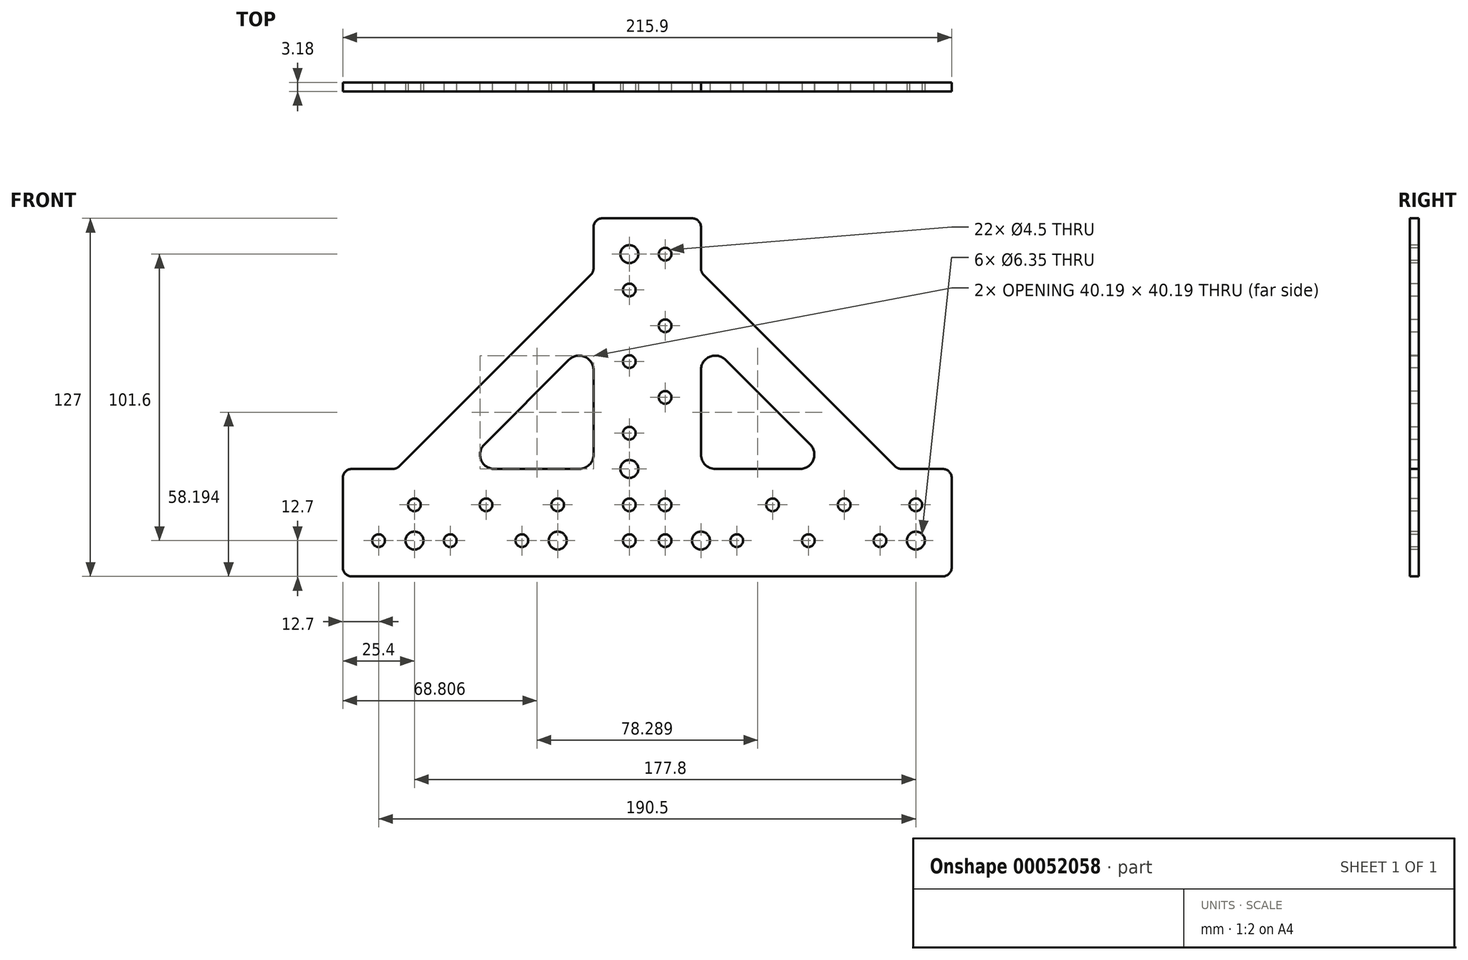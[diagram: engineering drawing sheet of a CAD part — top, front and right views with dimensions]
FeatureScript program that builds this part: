
annotation { "Feature Type Name" : "Feature", "Feature Type Description" : "" }
export const myFeature = defineFeature(function(context is Context, id is Id, definition is map)
    precondition{}
    {
        {
            var Q0;
            Q0=qCreatedBy(makeId("Front.planeOp"),FACE);
            var sketch = newSketch(context, id + "F0", { "sketchPlane" : qUnion([Q0])});
            skLineSegment(sketch, "E0.rect.bottom", {"start": v(-63.5, 63.5) * mm, "end": v(-25.4, 63.5) * mm});
            skLineSegment(sketch, "E0.rect.top", {"start": v(-63.5, -63.5) * mm, "end": v(63.5, -63.5) * mm});
            skLineSegment(sketch, "E0.rect.left", {"start": v(-63.5, 63.5) * mm, "end": v(-63.5, 44.45) * mm});
            skLineSegment(sketch, "E0.rect.right", {"start": v(63.5, -25.4) * mm, "end": v(63.5, -63.5) * mm});
            skPoint(sketch, "E0.rect.middle", {"position": v(0, 0) * mm});
            skLineSegment(sketch, "E1", {"start": v(-25.4, 63.5) * mm, "end": v(-25.4, 44.45) * mm});
            skLineSegment(sketch, "E2", {"start": v(63.5, -25.4) * mm, "end": v(44.45, -25.4) * mm});
            skLineSegment(sketch, "E3", {"start": v(-25.4, 44.45) * mm, "end": v(44.45, -25.4) * mm});
            skLineSegment(sketch, "E4", {"start": v(-25.4, 22) * mm, "end": v(22, -25.4) * mm});
            skPoint(sketch, "E5.orphan", {"position": v(63.5, 63.5) * mm});
            skLineSegment(sketch, "E6.trimOffspring", {"start": v(-25.4, 22) * mm, "end": v(-25.4, -25.4) * mm});
            skLineSegment(sketch, "E7.trimOffspring", {"start": v(22, -25.4) * mm, "end": v(-25.4, -25.4) * mm});
            skLineSegment(sketch, "E8", {"start": v(-63.5, -25.4) * mm, "end": v(-110.9, -25.4) * mm});
            skLineSegment(sketch, "E9", {"start": v(-152.4, -25.4) * mm, "end": v(-152.4, -63.5) * mm});
            skLineSegment(sketch, "E10", {"start": v(-152.4, -63.5) * mm, "end": v(-63.5, -63.5) * mm});
            skLineSegment(sketch, "E11", {"start": v(-63.5, 44.45) * mm, "end": v(-133.35, -25.4) * mm});
            skLineSegment(sketch, "E12", {"start": v(-63.5, 22) * mm, "end": v(-110.9, -25.4) * mm});
            skLineSegment(sketch, "E13.trimOffspring", {"start": v(-63.5, 22) * mm, "end": v(-63.5, -25.4) * mm});
            skLineSegment(sketch, "E14.trimOffspring", {"start": v(-133.35, -25.4) * mm, "end": v(-152.4, -25.4) * mm});
            skSolve(sketch);
        }
        {
            var Q0;
            Q0=makeQuery(id+"F0.imprint","IMPRINT",FACE,{"disambiguationData":[TD([[makeQuery(id+"F0.imprint","IMPRINT",EDGE,{"derivedFrom":sQuery(id+"F0.wireOp",EDGE,"E0.rect.bottom")}),-1.0]])]});
            extrude(context, id + "F1", {"entities" : qUnion([Q0]), "depth" : 3.17 * mm});
        }
        {
            var Q0;
            Q0=makeQuery(id+"F1.opExtrude","SWEPT_EDGE",EDGE,{"disambiguationData":[OSD([sQuery(id+"F0.wireOp",EDGE,"E0.rect.bottom"),sQuery(id+"F0.wireOp",EDGE,"E1")])]});
            var Q1;
            Q1=makeQuery(id+"F1.opExtrude","SWEPT_EDGE",EDGE,{"disambiguationData":[OSD([sQuery(id+"F0.wireOp",EDGE,"E1"),sQuery(id+"F0.wireOp",EDGE,"E3")])]});
            var Q2;
            Q2=makeQuery(id+"F1.opExtrude","SWEPT_EDGE",EDGE,{"disambiguationData":[OSD([sQuery(id+"F0.wireOp",EDGE,"E2"),sQuery(id+"F0.wireOp",EDGE,"E3")])]});
            var Q3;
            Q3=makeQuery(id+"F1.opExtrude","SWEPT_EDGE",EDGE,{"disambiguationData":[OSD([sQuery(id+"F0.wireOp",EDGE,"E0.rect.right"),sQuery(id+"F0.wireOp",EDGE,"E2")])]});
            var Q4;
            Q4=makeQuery(id+"F1.opExtrude","SWEPT_EDGE",EDGE,{"disambiguationData":[OSD([sQuery(id+"F0.wireOp",EDGE,"E0.rect.top"),sQuery(id+"F0.wireOp",EDGE,"E0.rect.right")])]});
            var Q5;
            Q5=makeQuery(id+"F1.opExtrude","SWEPT_EDGE",EDGE,{"disambiguationData":[OSD([sQuery(id+"F0.wireOp",EDGE,"E0.rect.top"),sQuery(id+"F0.wireOp",EDGE,"E0.rect.left")])]});
            var Q6;
            Q6=makeQuery(id+"F1.opExtrude","SWEPT_EDGE",EDGE,{"disambiguationData":[OSD([sQuery(id+"F0.wireOp",EDGE,"E0.rect.bottom"),sQuery(id+"F0.wireOp",EDGE,"E0.rect.left")])]});
            var Q7;
            Q7=makeQuery(id+"F1.opExtrude","SWEPT_EDGE",EDGE,{"disambiguationData":[OSD([sQuery(id+"F0.wireOp",EDGE,"E11"),sQuery(id+"F0.wireOp",EDGE,"E14.trimOffspring")])]});
            var Q8;
            Q8=makeQuery(id+"F1.opExtrude","SWEPT_EDGE",EDGE,{"disambiguationData":[OSD([sQuery(id+"F0.wireOp",EDGE,"E9"),sQuery(id+"F0.wireOp",EDGE,"E14.trimOffspring")])]});
            var Q9;
            Q9=makeQuery(id+"F1.opExtrude","SWEPT_EDGE",EDGE,{"disambiguationData":[OSD([sQuery(id+"F0.wireOp",EDGE,"E9"),sQuery(id+"F0.wireOp",EDGE,"E10")])]});
            fillet(context, id + "F2", {"entities" : qUnion([Q0, Q1, Q2, Q3, Q4, Q5, Q6, Q7, Q8, Q9]), "radius" : 3.17 * mm, "tangentPropagation" : true, "allowEdgeOverflow" : false});
        }
        {
            var Q0;
            Q0=makeQuery(id+"F1.opExtrude","SWEPT_EDGE",EDGE,{"disambiguationData":[OSD([sQuery(id+"F0.wireOp",EDGE,"E4"),sQuery(id+"F0.wireOp",EDGE,"E7.trimOffspring")])]});
            var Q1;
            Q1=makeQuery(id+"F1.opExtrude","SWEPT_EDGE",EDGE,{"disambiguationData":[OSD([sQuery(id+"F0.wireOp",EDGE,"E6.trimOffspring"),sQuery(id+"F0.wireOp",EDGE,"E7.trimOffspring")])]});
            var Q2;
            Q2=makeQuery(id+"F1.opExtrude","SWEPT_EDGE",EDGE,{"disambiguationData":[OSD([sQuery(id+"F0.wireOp",EDGE,"E4"),sQuery(id+"F0.wireOp",EDGE,"E6.trimOffspring")])]});
            fillet(context, id + "F3", {"entities" : qUnion([Q0, Q1, Q2]), "radius" : 5.08 * mm, "tangentPropagation" : true, "allowEdgeOverflow" : false});
        }
        {
            var Q0;
            Q0=makeQuery(id+"F1.opExtrude","CAP_FACE",FACE,{"disambiguationData":[OSD([sQuery(id+"F0.wireOp",EDGE,"E0.rect.bottom"),sQuery(id+"F0.wireOp",EDGE,"E0.rect.top"),sQuery(id+"F0.wireOp",EDGE,"E0.rect.left"),sQuery(id+"F0.wireOp",EDGE,"E0.rect.right"),sQuery(id+"F0.wireOp",EDGE,"E1"),sQuery(id+"F0.wireOp",EDGE,"E2"),sQuery(id+"F0.wireOp",EDGE,"E3"),sQuery(id+"F0.wireOp",EDGE,"E4"),sQuery(id+"F0.wireOp",EDGE,"E6.trimOffspring"),sQuery(id+"F0.wireOp",EDGE,"E7.trimOffspring")])],"isStart":false});
            var sketch = newSketch(context, id + "F4", { "sketchPlane" : qUnion([Q0])});
            skLineSegment(sketch, "E15", {"start": v(-50.8, 66.32) * mm, "end": v(-50.8, -65.15) * mm, "construction": true});
            skLineSegment(sketch, "E16", {"start": v(65.1, -50.8) * mm, "end": v(-158.46, -50.8) * mm, "construction": true});
            skLineSegment(sketch, "E17", {"start": v(-38.1, 66.32) * mm, "end": v(-38.1, -66.32) * mm, "construction": true});
            skLineSegment(sketch, "E18", {"start": v(73.12, -38.1) * mm, "end": v(-159.28, -38.1) * mm, "construction": true});
            skPoint(sketch, "E19", {"position": v(-50.8, -50.8) * mm});
            skPoint(sketch, "E20", {"position": v(-50.8, -38.1) * mm});
            skPoint(sketch, "E21", {"position": v(-38.1, -38.1) * mm});
            skPoint(sketch, "E22", {"position": v(-38.1, -50.8) * mm});
            skPoint(sketch, "E23", {"position": v(-50.8, 50.8) * mm});
            skPoint(sketch, "E24", {"position": v(-38.1, 50.8) * mm});
            skPoint(sketch, "E25", {"position": v(-50.8, 38.1) * mm});
            skPoint(sketch, "E26", {"position": v(-38.1, 25.4) * mm});
            skPoint(sketch, "E27", {"position": v(-50.8, 12.7) * mm});
            skPoint(sketch, "E28", {"position": v(-38.1, 0) * mm});
            skPoint(sketch, "E29", {"position": v(-50.8, -12.7) * mm});
            skPoint(sketch, "E30", {"position": v(-50.8, -25.4) * mm});
            skPoint(sketch, "E31", {"position": v(50.8, -50.8) * mm});
            skPoint(sketch, "E32", {"position": v(50.8, -38.1) * mm});
            skPoint(sketch, "E33", {"position": v(38.1, -50.8) * mm});
            skPoint(sketch, "E34", {"position": v(12.7, -50.8) * mm});
            skPoint(sketch, "E35", {"position": v(-12.7, -50.8) * mm});
            skPoint(sketch, "E36", {"position": v(-25.4, -50.8) * mm});
            skPoint(sketch, "E37", {"position": v(25.4, -38.1) * mm});
            skPoint(sketch, "E38", {"position": v(0, -38.1) * mm});
            skPoint(sketch, "E39", {"position": v(-127, -38.1) * mm});
            skPoint(sketch, "E40", {"position": v(-139.7, -50.8) * mm});
            skPoint(sketch, "E41", {"position": v(-101.6, -38.1) * mm});
            skPoint(sketch, "E42", {"position": v(-76.2, -38.1) * mm});
            skPoint(sketch, "E43", {"position": v(-127, -50.8) * mm});
            skPoint(sketch, "E44", {"position": v(-88.9, -50.8) * mm});
            skPoint(sketch, "E45", {"position": v(-76.2, -50.8) * mm});
            skPoint(sketch, "E46", {"position": v(-114.3, -50.8) * mm});
            skSolve(sketch);
        }
        {
            var Q0;
            Q0=sQuery(id+"F4.wireOp",VERTEX,"E23");
            var Q1;
            Q1=sQuery(id+"F4.wireOp",VERTEX,"E30");
            var Q2;
            Q2=sQuery(id+"F4.wireOp",VERTEX,"E31");
            var Q3;
            Q3=sQuery(id+"F4.wireOp",VERTEX,"E36");
            var Q4;
            Q4=sQuery(id+"F4.wireOp",VERTEX,"E45");
            var Q5;
            Q5=sQuery(id+"F4.wireOp",VERTEX,"E43");
            var Q6;
            Q6=makeQuery(id+"F1.opExtrude","SWEPT_BODY",BODY,{"disambiguationData":[OSD([sQuery(id+"F0.wireOp",EDGE,"E0.rect.bottom"),sQuery(id+"F0.wireOp",EDGE,"E0.rect.top"),sQuery(id+"F0.wireOp",EDGE,"E0.rect.left"),sQuery(id+"F0.wireOp",EDGE,"E0.rect.right"),sQuery(id+"F0.wireOp",EDGE,"E1"),sQuery(id+"F0.wireOp",EDGE,"E2"),sQuery(id+"F0.wireOp",EDGE,"E3"),sQuery(id+"F0.wireOp",EDGE,"E4"),sQuery(id+"F0.wireOp",EDGE,"E6.trimOffspring"),sQuery(id+"F0.wireOp",EDGE,"E7.trimOffspring")])]});
            hole(context, id + "F5", {"style" : HoleStyle.SIMPLE, "holeDiameter" : 6.35 * mm, "endStyle" : HoleEndStyle.THROUGH, "locations" : qUnion([Q0, Q1, Q2, Q3, Q4, Q5]), "scope" : qUnion([Q6])});
        }
        {
            var Q0;
            Q0=sQuery(id+"F4.wireOp",VERTEX,"E25");
            var Q1;
            Q1=sQuery(id+"F4.wireOp",VERTEX,"E24");
            var Q2;
            Q2=sQuery(id+"F4.wireOp",VERTEX,"E26");
            var Q3;
            Q3=sQuery(id+"F4.wireOp",VERTEX,"E27");
            var Q4;
            Q4=sQuery(id+"F4.wireOp",VERTEX,"E28");
            var Q5;
            Q5=sQuery(id+"F4.wireOp",VERTEX,"E29");
            var Q6;
            Q6=sQuery(id+"F4.wireOp",VERTEX,"E21");
            var Q7;
            Q7=sQuery(id+"F4.wireOp",VERTEX,"E20");
            var Q8;
            Q8=sQuery(id+"F4.wireOp",VERTEX,"E19");
            var Q9;
            Q9=sQuery(id+"F4.wireOp",VERTEX,"E22");
            var Q10;
            Q10=sQuery(id+"F4.wireOp",VERTEX,"E35");
            var Q11;
            Q11=sQuery(id+"F4.wireOp",VERTEX,"E38");
            var Q12;
            Q12=sQuery(id+"F4.wireOp",VERTEX,"E34");
            var Q13;
            Q13=sQuery(id+"F4.wireOp",VERTEX,"E37");
            var Q14;
            Q14=sQuery(id+"F4.wireOp",VERTEX,"E33");
            var Q15;
            Q15=sQuery(id+"F4.wireOp",VERTEX,"E32");
            var Q16;
            Q16=sQuery(id+"F4.wireOp",VERTEX,"E40");
            var Q17;
            Q17=sQuery(id+"F4.wireOp",VERTEX,"E39");
            var Q18;
            Q18=sQuery(id+"F4.wireOp",VERTEX,"E46");
            var Q19;
            Q19=sQuery(id+"F4.wireOp",VERTEX,"E41");
            var Q20;
            Q20=sQuery(id+"F4.wireOp",VERTEX,"E44");
            var Q21;
            Q21=sQuery(id+"F4.wireOp",VERTEX,"E42");
            var Q22;
            Q22=makeQuery(id+"F1.opExtrude","SWEPT_BODY",BODY,{"disambiguationData":[OSD([sQuery(id+"F0.wireOp",EDGE,"E0.rect.bottom"),sQuery(id+"F0.wireOp",EDGE,"E0.rect.top"),sQuery(id+"F0.wireOp",EDGE,"E0.rect.left"),sQuery(id+"F0.wireOp",EDGE,"E0.rect.right"),sQuery(id+"F0.wireOp",EDGE,"E1"),sQuery(id+"F0.wireOp",EDGE,"E2"),sQuery(id+"F0.wireOp",EDGE,"E3"),sQuery(id+"F0.wireOp",EDGE,"E4"),sQuery(id+"F0.wireOp",EDGE,"E6.trimOffspring"),sQuery(id+"F0.wireOp",EDGE,"E7.trimOffspring")])]});
            hole(context, id + "F6", {"style" : HoleStyle.SIMPLE, "holeDiameter" : 4.5 * mm, "endStyle" : HoleEndStyle.THROUGH, "locations" : qUnion([Q0, Q1, Q2, Q3, Q4, Q5, Q6, Q7, Q8, Q9, Q10, Q11, Q12, Q13, Q14, Q15, Q16, Q17, Q18, Q19, Q20, Q21]), "scope" : qUnion([Q22])});
        }
        {
            var Q0;
            Q0=makeQuery(id+"F1.opExtrude","SWEPT_EDGE",EDGE,{"disambiguationData":[OSD([sQuery(id+"F0.wireOp",EDGE,"E8"),sQuery(id+"F0.wireOp",EDGE,"E12")])]});
            var Q1;
            Q1=makeQuery(id+"F1.opExtrude","SWEPT_EDGE",EDGE,{"disambiguationData":[OSD([sQuery(id+"F0.wireOp",EDGE,"E8"),sQuery(id+"F0.wireOp",EDGE,"E13.trimOffspring")])]});
            var Q2;
            Q2=makeQuery(id+"F1.opExtrude","SWEPT_EDGE",EDGE,{"disambiguationData":[OSD([sQuery(id+"F0.wireOp",EDGE,"E12"),sQuery(id+"F0.wireOp",EDGE,"E13.trimOffspring")])]});
            fillet(context, id + "F7", {"entities" : qUnion([Q0, Q1, Q2]), "radius" : 5.08 * mm, "tangentPropagation" : true, "allowEdgeOverflow" : false});
        }
    });
